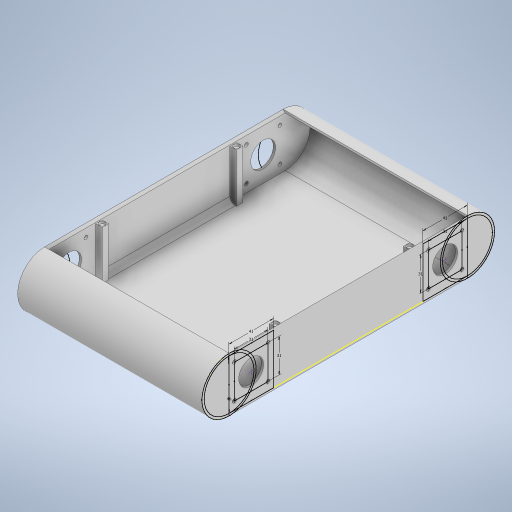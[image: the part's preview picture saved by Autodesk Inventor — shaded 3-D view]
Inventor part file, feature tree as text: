
AUTODESK INVENTOR PART (.ipt)
format: ipt  version: 2024 (Build 280153020, 153B)  size: 373,760 bytes
history: native  units: mm
features: extrude x6, hole x4, sketch x4, other x2, chamfer x1, fillet x1
ambient origin geometry x8: Origin, YZ Plane, XZ Plane, XY Plane, X Axis, Y Axis, Z Axis, Center Point
bodies: Solid1 (feature_tree)
feature tree (18):
  extrude  "base"  Depth=220.0mm
  extrude  "walls"  Depth=2.0mm
  other  "rounded_wall"
  extrude  "rounded_wall_extrusion"  Depth=2.0mm TaperAngle=0.0deg
  extrude  "rounded_wall_side1_extrusion"  Depth=170.0mm TaperAngle=0.0deg
  extrude  "rounded_wall_side2_extrusion"  Depth=2.0mm TaperAngle=0.0deg
  hole  "holes"  [1 undecoded]
  hole  "shaft_holes"  [1 undecoded]
  hole  "motor_holes"  [1 undecoded]
  extrude  "columns"  Depth=5.0mm
  hole  "magnet_holders"  [1 undecoded]
  chamfer  "chamfers"  Distance=31.0mm
  fillet  "fillets"  Radius=31.0mm
  sketch  "Sketch1"  dims[d0=170.0mm d1=220.0mm]
  sketch  "Sketch2"  dims[d2=2.0mm d3=0.0mm d4=2.0mm]
  other  "rounded_wall_side2"
  sketch  "Sketch7"  dims[d5=2.0mm d6=48.0mm d7=0.0mm]
  sketch  "Sketch9"  dims[d8=46.0mm d9=170.0mm d10=0.0mm d11=2.0mm d12=0.0mm d13=2.0mm d14=0.0mm d15=41.0mm d16=41.0mm d17=31.0mm d18=31.0mm d19=31.0mm d20=31.0mm d21=23.0mm d22=6.0mm d23=4.0mm d24=2.0mm d25=90.0deg d26=8.0mm d27=20.594885mm d28=3.5mm d29=6.0mm d30=4.0mm d31=2.0mm d32=90.0deg d33=8.0mm d34=20.594885mm d35=130.0mm d36=6.0mm d37=6.0mm d38=6.0mm d39=6.0mm d40=6.0mm d41=6.0mm d42=45.0mm d43=0.0mm d44=5.5mm d45=6.0mm d46=4.0mm d47=2.0mm d48=90.0deg d49=2.0mm d50=0.0mm d51=2.0mm d52=2.0mm d53=45.0deg d57=5.0mm]
note: 4 required parameter values undecoded (feature->parameter linkage not recoverable at this tier; creation-order binding heuristic only, values carry confidence <= 0.55)
